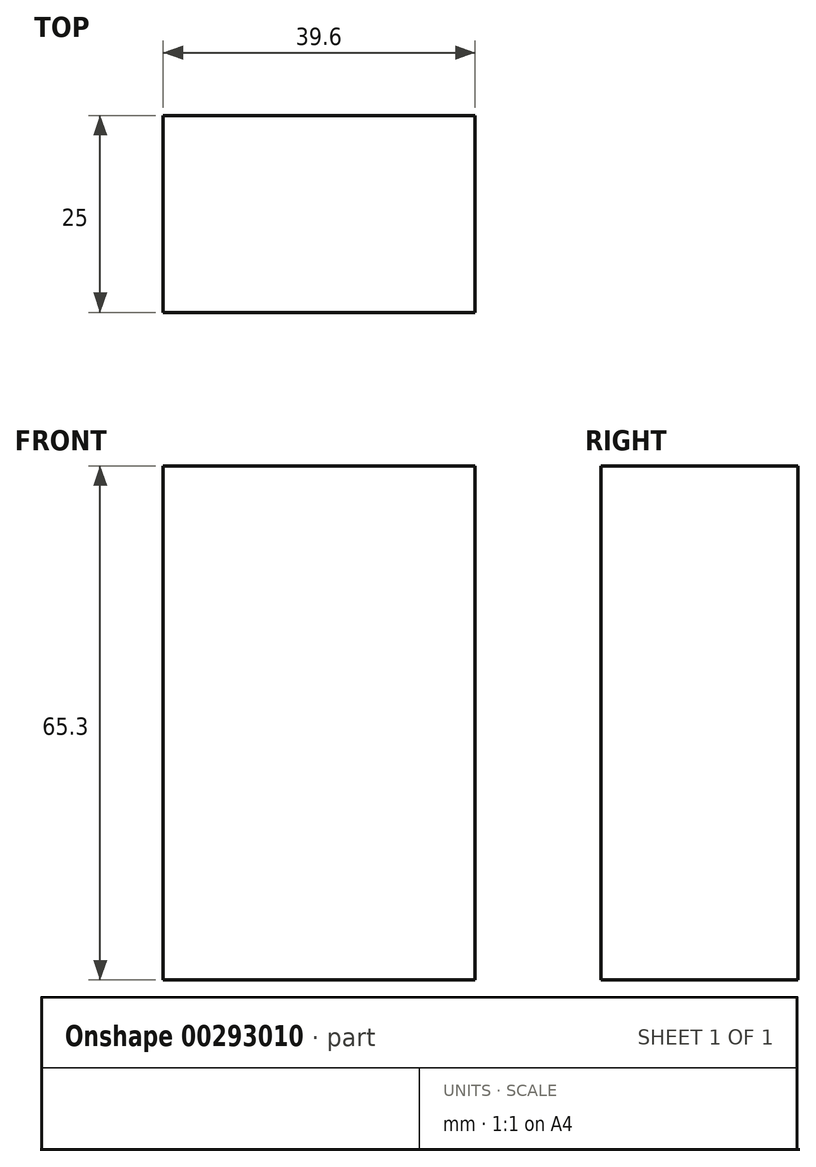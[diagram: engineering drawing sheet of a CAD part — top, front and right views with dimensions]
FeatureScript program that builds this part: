
annotation { "Feature Type Name" : "Feature", "Feature Type Description" : "" }
export const myFeature = defineFeature(function(context is Context, id is Id, definition is map)
    precondition{}
    {
        {
            var Q0;
            Q0=qCreatedBy(makeId("Front.planeOp"),FACE);
            var sketch = newSketch(context, id + "F0", { "sketchPlane" : qUnion([Q0])});
            skLineSegment(sketch, "E0.bottom", {"start": v(-80.5, 11.17) * mm, "end": v(-40.9, 11.17) * mm});
            skLineSegment(sketch, "E0.top", {"start": v(-80.5, 76.47) * mm, "end": v(-40.9, 76.47) * mm});
            skLineSegment(sketch, "E0.left", {"start": v(-80.5, 11.17) * mm, "end": v(-80.5, 76.47) * mm});
            skLineSegment(sketch, "E0.right", {"start": v(-40.9, 11.17) * mm, "end": v(-40.9, 76.47) * mm});
            skPoint(sketch, "E0.middle", {"position": v(-60.7, 43.82) * mm});
            skSolve(sketch);
        }
        {
            var Q0;
            Q0=makeQuery(id+"F0.imprint","IMPRINT",FACE,{"disambiguationData":[TD([[makeQuery(id+"F0.imprint","IMPRINT",EDGE,{"derivedFrom":sQuery(id+"F0.wireOp",EDGE,"E0.bottom")}),1.0]])]});
            extrude(context, id + "F1", {"entities" : qUnion([Q0]), "depth" : 25 * mm});
        }
    });
